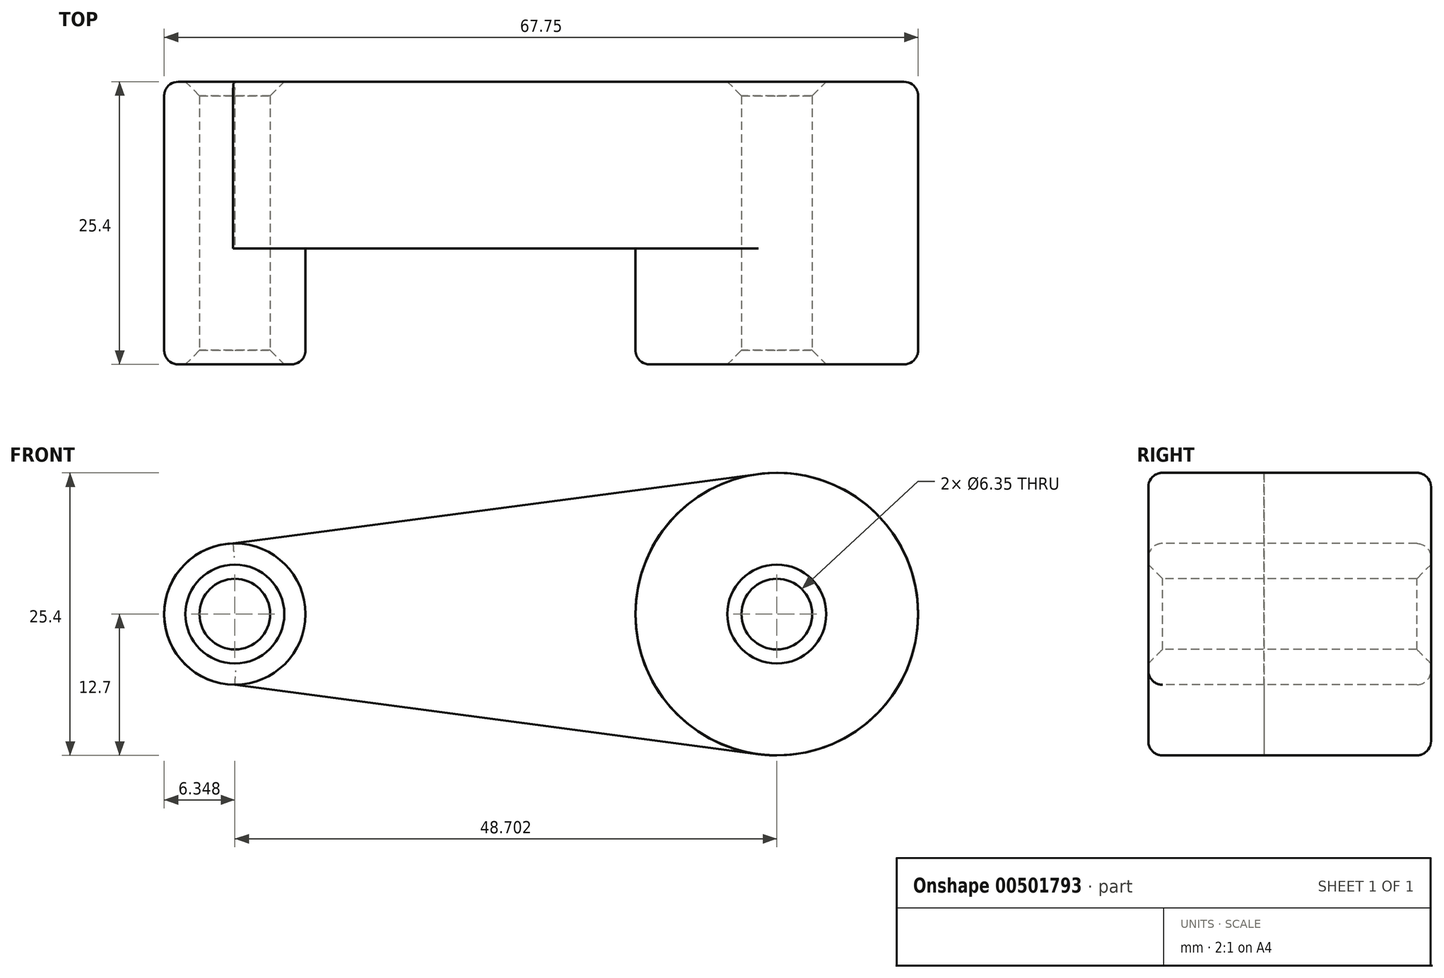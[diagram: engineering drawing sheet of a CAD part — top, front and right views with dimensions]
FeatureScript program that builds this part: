
annotation { "Feature Type Name" : "Feature", "Feature Type Description" : "" }
export const myFeature = defineFeature(function(context is Context, id is Id, definition is map)
    precondition{}
    {
        {
            var Q0;
            Q0=qCreatedBy(makeId("Front.planeOp"),FACE);
            var sketch = newSketch(context, id + "F0", { "sketchPlane" : qUnion([Q0])});
            skCircle(sketch, "E0", {"center": v(0, 0) * mm, "radius": 12.7 * mm});
            skCircle(sketch, "E1", {"center": v(-48.7, 0) * mm, "radius": 6.35 * mm});
            skCircle(sketch, "E2", {"center": v(-48.7, 0) * mm, "radius": 3.18 * mm});
            skCircle(sketch, "E3", {"center": v(0, 0) * mm, "radius": 3.18 * mm});
            skLineSegment(sketch, "E4", {"start": v(-48.87, 6.35) * mm, "end": v(0, 12.81) * mm});
            skLineSegment(sketch, "E5", {"start": v(-48.7, -6.35) * mm, "end": v(0, -12.81) * mm});
            skLineSegment(sketch, "E6", {"start": v(6.38, 10.98) * mm, "end": v(9.08, 8.88) * mm});
            skPoint(sketch, "E7.orphan", {"position": v(36.93, -12.81) * mm});
            skSolve(sketch);
        }
        {
            var Q0;
            Q0 = qSketchRegion(id + "F0", true);
            extrude(context, id + "F1", {"entities" : qUnion([Q0]), "oppositeDirection" : true, "depth" : 25.4 * mm});
        }
        {
            var Q0;
            {var subQ0=sQuery(id+"F0.wireOp",EDGE,"E4");var subQ1=sQuery(id+"F0.wireOp",EDGE,"E0");var subQ2=makeQuery(id+"F0.imprint","INTERSECT",VERTEX,{"derivedFrom":[subQ1,subQ0]});Q0=makeQuery(id+"F0.imprint","IMPRINT",FACE,{"disambiguationData":[TD([[makeQuery(id+"F0.imprint","IMPRINT",EDGE,{"disambiguationData":[TD([[subQ2,-1.0]])],"derivedFrom":subQ1}),-1.0]])]});}
            extrude(context, id + "F2", {"entities" : qUnion([Q0]), "operationType" : NewBodyOperationType.REMOVE, "endBound" : BoundingType.SYMMETRIC, "oppositeDirection" : true, "depth" : 20.83 * mm, "offsetDistance" : 25.4 * mm});
        }
        {
            var Q0;
            Q0=makeQuery(id+"F1.opExtrude","CAP_EDGE",EDGE,{"disambiguationData":[OSD([sQuery(id+"F0.wireOp",EDGE,"E3")])],"isStart":true});
            chamfer(context, id + "F3", {"entities" : qUnion([Q0]), "width" : 1.27 * mm, "tangentPropagation" : true});
        }
        {
            var Q0;
            Q0=makeQuery(id+"F1.opExtrude","CAP_EDGE",EDGE,{"disambiguationData":[OSD([sQuery(id+"F0.wireOp",EDGE,"E2")])],"isStart":true});
            var Q1;
            Q1=makeQuery(id+"F1.opExtrude","CAP_EDGE",EDGE,{"disambiguationData":[OSD([sQuery(id+"F0.wireOp",EDGE,"E3")])],"isStart":false});
            var Q2;
            Q2=makeQuery(id+"F1.opExtrude","CAP_EDGE",EDGE,{"disambiguationData":[OSD([sQuery(id+"F0.wireOp",EDGE,"E2")])],"isStart":false});
            chamfer(context, id + "F4", {"entities" : qUnion([Q0, Q1, Q2]), "width" : 1.27 * mm, "tangentPropagation" : true});
        }
        {
            var Q0;
            Q0=makeQuery(id+"F1.opExtrude","CAP_EDGE",EDGE,{"disambiguationData":[OSD([sQuery(id+"F0.wireOp",EDGE,"E0")])],"isStart":false});
            var Q1;
            Q1=makeQuery(id+"F1.opExtrude","CAP_EDGE",EDGE,{"disambiguationData":[OSD([sQuery(id+"F0.wireOp",EDGE,"E1")])],"isStart":false});
            var Q2;
            {var subQ0=sQuery(id+"F0.wireOp",EDGE,"E0");Q2=makeQuery(id+"F2.boolean.opBoolean","INTERSECT",EDGE,{"derivedFrom":[makeQuery(id+"F1.opExtrude","CAP_FACE",FACE,{"disambiguationData":[OSD([subQ0,sQuery(id+"F0.wireOp",EDGE,"E1"),sQuery(id+"F0.wireOp",EDGE,"E2"),sQuery(id+"F0.wireOp",EDGE,"E3"),sQuery(id+"F0.wireOp",EDGE,"E4"),sQuery(id+"F0.wireOp",EDGE,"E5")])],"isStart":true}),makeQuery(id+"F2.opExtrude","SWEPT_FACE",FACE,{"disambiguationData":[OSD([subQ0])]})]});}
            var Q3;
            {var subQ0=sQuery(id+"F0.wireOp",EDGE,"E1");Q3=makeQuery(id+"F2.boolean.opBoolean","INTERSECT",EDGE,{"derivedFrom":[makeQuery(id+"F1.opExtrude","CAP_FACE",FACE,{"disambiguationData":[OSD([sQuery(id+"F0.wireOp",EDGE,"E0"),subQ0,sQuery(id+"F0.wireOp",EDGE,"E2"),sQuery(id+"F0.wireOp",EDGE,"E3"),sQuery(id+"F0.wireOp",EDGE,"E4"),sQuery(id+"F0.wireOp",EDGE,"E5")])],"isStart":true}),makeQuery(id+"F2.opExtrude","SWEPT_FACE",FACE,{"disambiguationData":[OSD([subQ0])]})]});}
            var Q4;
            Q4=makeQuery(id+"F2.boolean.opBoolean","COPY",EDGE,{"derivedFrom":makeQuery(id+"F2.opExtrude","CAP_EDGE",EDGE,{"disambiguationData":[OSD([sQuery(id+"F0.wireOp",EDGE,"E4")])],"isStart":false})});
            var Q5;
            Q5=makeQuery(id+"F2.boolean.opBoolean","COPY",EDGE,{"derivedFrom":makeQuery(id+"F2.opExtrude","CAP_EDGE",EDGE,{"disambiguationData":[OSD([sQuery(id+"F0.wireOp",EDGE,"E5")])],"isStart":false})});
            fillet(context, id + "F5", {"entities" : qUnion([Q0, Q1, Q2, Q3, Q4, Q5]), "radius" : 1.27 * mm, "tangentPropagation" : true, "allowEdgeOverflow" : false});
        }
    });
